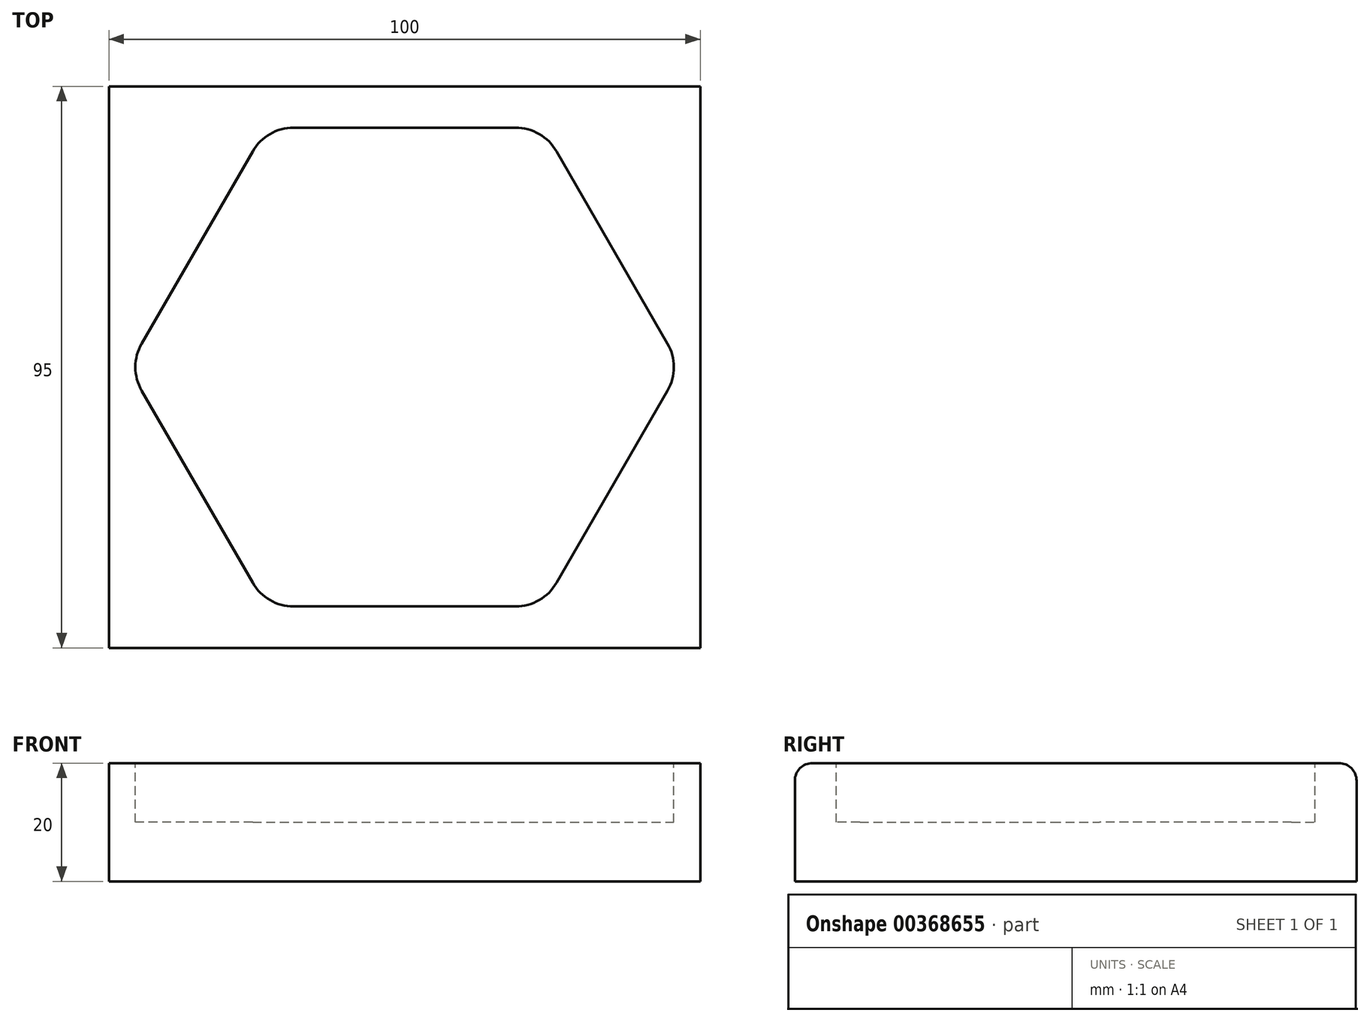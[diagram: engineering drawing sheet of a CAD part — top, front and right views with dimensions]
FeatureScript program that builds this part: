
annotation { "Feature Type Name" : "Feature", "Feature Type Description" : "" }
export const myFeature = defineFeature(function(context is Context, id is Id, definition is map)
    precondition{}
    {
        {
            var Q0;
            Q0=qCreatedBy(makeId("Top.planeOp"),FACE);
            var sketch = newSketch(context, id + "F0", { "sketchPlane" : qUnion([Q0])});
            skLineSegment(sketch, "E0.bottom", {"start": v(50, 47.5) * mm, "end": v(-50, 47.5) * mm});
            skLineSegment(sketch, "E0.top", {"start": v(50, -47.5) * mm, "end": v(-50, -47.5) * mm});
            skLineSegment(sketch, "E0.left", {"start": v(50, 47.5) * mm, "end": v(50, -47.5) * mm});
            skLineSegment(sketch, "E0.right", {"start": v(-50, 47.5) * mm, "end": v(-50, -47.5) * mm});
            skPoint(sketch, "E0.middle", {"position": v(0, 0) * mm});
            skSolve(sketch);
        }
        {
            var Q0;
            Q0=makeQuery(id+"F0.imprint","IMPRINT",FACE,{"disambiguationData":[TD([[makeQuery(id+"F0.imprint","IMPRINT",EDGE,{"derivedFrom":sQuery(id+"F0.wireOp",EDGE,"E0.bottom")}),1.0]])]});
            extrude(context, id + "F1", {"entities" : qUnion([Q0]), "endBound" : BoundingType.SYMMETRIC, "depth" : 20 * mm});
        }
        {
            var Q0;
            Q0=makeQuery(id+"F1.opExtrude","CAP_FACE",FACE,{"disambiguationData":[OSD([sQuery(id+"F0.wireOp",EDGE,"E0.bottom"),sQuery(id+"F0.wireOp",EDGE,"E0.top"),sQuery(id+"F0.wireOp",EDGE,"E0.left"),sQuery(id+"F0.wireOp",EDGE,"E0.right")])],"isStart":false});
            var sketch = newSketch(context, id + "F2", { "sketchPlane" : qUnion([Q0])});
            skLineSegment(sketch, "E1", {"start": v(0, 0) * mm, "end": v(-37.53, 0) * mm, "construction": true});
            skLineSegment(sketch, "E2", {"start": v(0, 0) * mm, "end": v(-18.76, 32.5) * mm, "construction": true});
            skLineSegment(sketch, "E3", {"start": v(-18.76, 32.5) * mm, "end": v(-37.53, 0) * mm, "construction": true});
            skLineSegment(sketch, "E4.MirrorCS", {"start": v(-18.76, -32.5) * mm, "end": v(-37.53, 0) * mm, "construction": true});
            skLineSegment(sketch, "E5.MirrorCS", {"start": v(0, 0) * mm, "end": v(-18.76, -32.5) * mm, "construction": true});
            skLineSegment(sketch, "E6", {"start": v(0, -8) * mm, "end": v(0, 6.86) * mm, "construction": true});
            skLineSegment(sketch, "E7.MirrorCS", {"start": v(0, 0) * mm, "end": v(18.76, 32.5) * mm, "construction": true});
            skLineSegment(sketch, "E8.MirrorCS", {"start": v(18.76, 32.5) * mm, "end": v(37.53, 0) * mm, "construction": true});
            skLineSegment(sketch, "E9.MirrorCS", {"start": v(0, 0) * mm, "end": v(37.53, 0) * mm, "construction": true});
            skLineSegment(sketch, "E10.MirrorCS", {"start": v(0, 0) * mm, "end": v(18.76, -32.5) * mm, "construction": true});
            skLineSegment(sketch, "E11.MirrorCS", {"start": v(18.76, -32.5) * mm, "end": v(37.53, 0) * mm, "construction": true});
            skLineSegment(sketch, "E12", {"start": v(-18.76, 32.5) * mm, "end": v(18.76, 32.5) * mm, "construction": true});
            skLineSegment(sketch, "E13", {"start": v(-18.76, -32.5) * mm, "end": v(18.76, -32.5) * mm, "construction": true});
            skLineSegment(sketch, "E14.0", {"start": v(-23.38, 40.5) * mm, "end": v(23.38, 40.5) * mm});
            skLineSegment(sketch, "E14.1", {"start": v(-23.38, -40.5) * mm, "end": v(-46.77, 0) * mm});
            skLineSegment(sketch, "E14.2", {"start": v(-23.38, -40.5) * mm, "end": v(23.38, -40.5) * mm});
            skLineSegment(sketch, "E14.3", {"start": v(-23.38, 40.5) * mm, "end": v(-46.77, 0) * mm});
            skLineSegment(sketch, "E14.4", {"start": v(23.38, -40.5) * mm, "end": v(46.77, 0) * mm});
            skLineSegment(sketch, "E14.5", {"start": v(23.38, 40.5) * mm, "end": v(46.77, 0) * mm});
            skLineSegment(sketch, "E15", {"start": v(-18.76, 32.5) * mm, "end": v(-18.76, 40.5) * mm, "construction": true});
            skLineSegment(sketch, "E16", {"start": v(-18.76, 32.5) * mm, "end": v(-23.38, 40.5) * mm, "construction": true});
            skLineSegment(sketch, "E17", {"start": v(-18.76, 32.5) * mm, "end": v(-25.7, 36.5) * mm, "construction": true});
            skLineSegment(sketch, "E18", {"start": v(-18.76, 40.5) * mm, "end": v(-23.38, 40.5) * mm});
            skArc(sketch, "E19", {"start": v(-18.76, 40.5) * mm, "mid": v(-22.76, 39.43) * mm, "end": v(-25.7, 36.5) * mm});
            skArc(sketch, "E20.MirrorCS", {"start": v(18.76, 40.5) * mm, "mid": v(22.76, 39.43) * mm, "end": v(25.7, 36.5) * mm});
            skArc(sketch, "E21.MirrorCS", {"start": v(-18.76, -40.5) * mm, "mid": v(-22.76, -39.43) * mm, "end": v(-25.7, -36.5) * mm});
            skArc(sketch, "E22.MirrorCS", {"start": v(18.76, -40.5) * mm, "mid": v(22.76, -39.43) * mm, "end": v(25.7, -36.5) * mm});
            skLineSegment(sketch, "E23", {"start": v(-37.53, 0) * mm, "end": v(-46.77, 0) * mm, "construction": true});
            skLineSegment(sketch, "E24", {"start": v(-37.53, 0) * mm, "end": v(-44.46, 4) * mm, "construction": true});
            skLineSegment(sketch, "E25", {"start": v(-37.53, 0) * mm, "end": v(-44.46, -4) * mm, "construction": true});
            skArc(sketch, "E26", {"start": v(-44.46, 4) * mm, "mid": v(-45.53, 0) * mm, "end": v(-44.46, -4) * mm});
            skArc(sketch, "E27.MirrorCS", {"start": v(44.46, 4) * mm, "mid": v(45.53, 0) * mm, "end": v(44.46, -4) * mm});
            skSolve(sketch);
        }
        {
            var Q0;
            {var subQ2=sQuery(id+"F2.wireOp",EDGE,"E19");Q0=makeQuery(id+"F2.imprint","IMPRINT",FACE,{"disambiguationData":[TD([[makeQuery(id+"F2.imprint","IMPRINT",EDGE,{"derivedFrom":subQ2}),1.0]])]});}
            extrude(context, id + "F3", {"entities" : qUnion([Q0]), "operationType" : NewBodyOperationType.REMOVE, "oppositeDirection" : true, "depth" : 10 * mm});
        }
        {
            var Q0;
            Q0=makeQuery(id+"F1.opExtrude","CAP_EDGE",EDGE,{"disambiguationData":[OSD([sQuery(id+"F0.wireOp",EDGE,"E0.top")])],"isStart":false});
            var Q1;
            Q1=makeQuery(id+"F1.opExtrude","CAP_EDGE",EDGE,{"disambiguationData":[OSD([sQuery(id+"F0.wireOp",EDGE,"E0.bottom")])],"isStart":false});
            fillet(context, id + "F4", {"entities" : qUnion([Q0, Q1]), "radius" : 3 * mm, "tangentPropagation" : true, "allowEdgeOverflow" : false});
        }
    });
